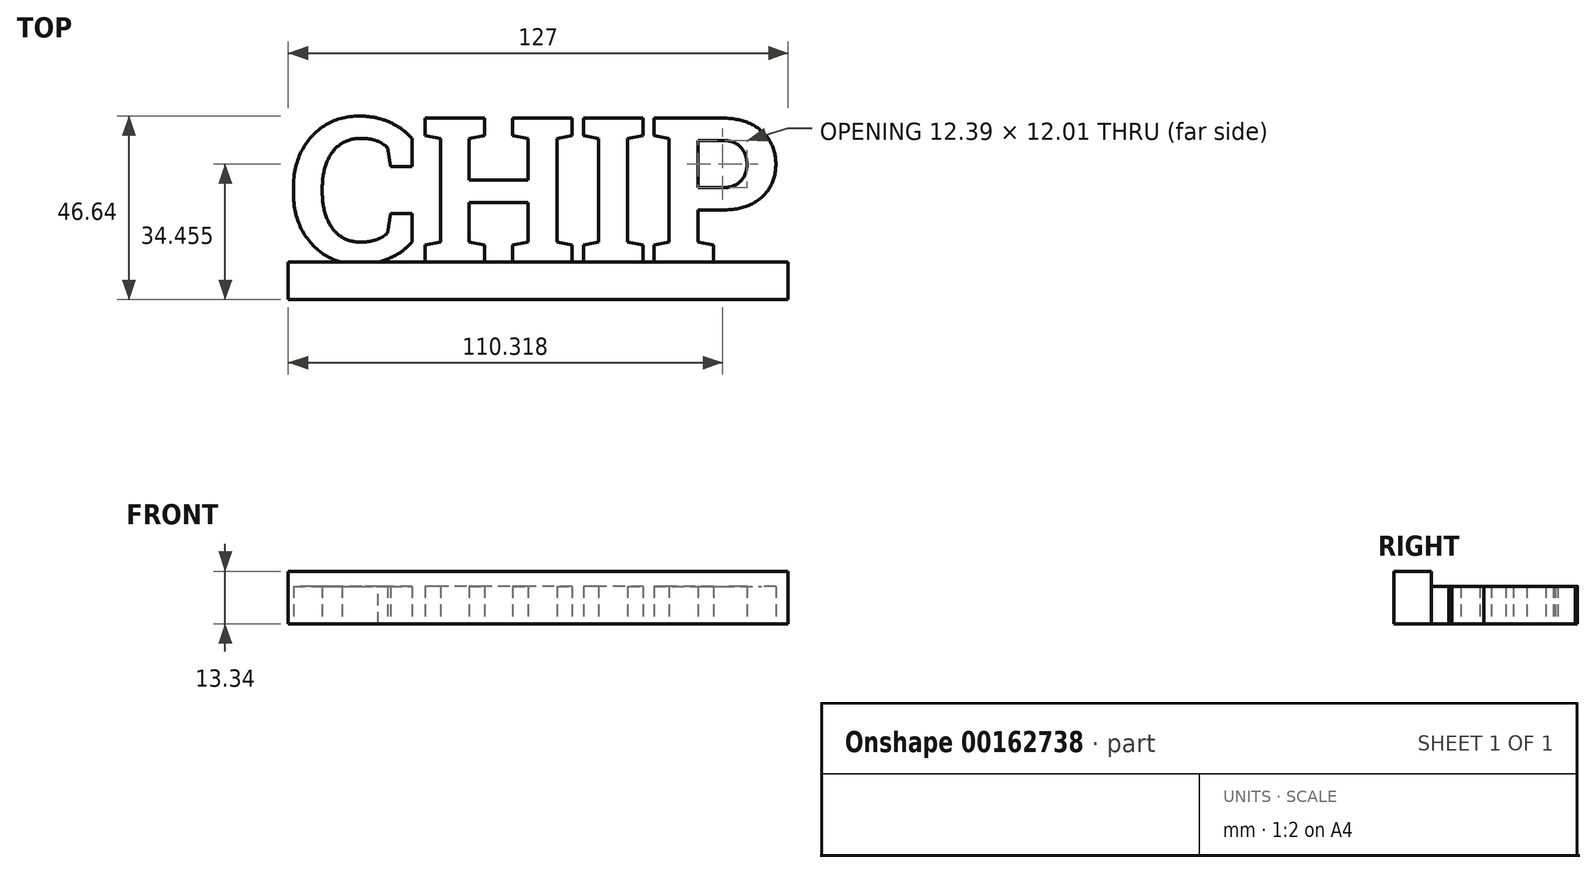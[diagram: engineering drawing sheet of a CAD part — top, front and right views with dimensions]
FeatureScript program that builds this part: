
annotation { "Feature Type Name" : "Feature", "Feature Type Description" : "" }
export const myFeature = defineFeature(function(context is Context, id is Id, definition is map)
    precondition{}
    {
        {
            var Q0;
            Q0=qCreatedBy(makeId("Top.planeOp"),FACE);
            var sketch = newSketch(context, id + "F0", { "sketchPlane" : qUnion([Q0])});
            skLineSegment(sketch, "E0.bottom", {"start": v(0, 0) * mm, "end": v(127, 0) * mm});
            skLineSegment(sketch, "E0.top", {"start": v(0, 9.53) * mm, "end": v(127, 9.53) * mm});
            skLineSegment(sketch, "E0.left", {"start": v(0, 0) * mm, "end": v(0, 9.53) * mm});
            skLineSegment(sketch, "E0.right", {"start": v(127, 0) * mm, "end": v(127, 9.53) * mm});
            skText(sketch, "E1", { "text": "CHIP", "fontName": "RobotoSlab-Bold.ttf"});
            const initialGuessF0  = {"E1": [0, 0.00953, 1, 0, 0.03705]};
            skSetInitialGuess(sketch, initialGuessF0);
            skSolve(sketch);
        }
        {
            var Q0;
            Q0 = qSketchRegion(id + "F0", true);
            extrude(context, id + "F1", {"entities" : qUnion([Q0]), "depth" : 9.52 * mm});
        }
        {
            var Q0;
            Q0=makeQuery(id+"F1.opExtrude","CAP_FACE",FACE,{"disambiguationData":[OSD([sQuery(id+"F0.wireOp",EDGE,"E0.bottom"),sQuery(id+"F0.wireOp",EDGE,"E0.top"),sQuery(id+"F0.wireOp",EDGE,"E0.left"),sQuery(id+"F0.wireOp",EDGE,"E0.right"),sQuery(id+"F0.wireOp",EDGE,"E1.sketch_text.stroke-0"),sQuery(id+"F0.wireOp",EDGE,"E1.sketch_text.stroke-1"),sQuery(id+"F0.wireOp",EDGE,"E1.sketch_text.stroke-2"),sQuery(id+"F0.wireOp",EDGE,"E1.sketch_text.stroke-3"),sQuery(id+"F0.wireOp",EDGE,"E1.sketch_text.stroke-4"),sQuery(id+"F0.wireOp",EDGE,"E1.sketch_text.stroke-5"),sQuery(id+"F0.wireOp",EDGE,"E1.sketch_text.stroke-6"),sQuery(id+"F0.wireOp",EDGE,"E1.sketch_text.stroke-7"),sQuery(id+"F0.wireOp",EDGE,"E1.sketch_text.stroke-8"),sQuery(id+"F0.wireOp",EDGE,"E1.sketch_text.stroke-9"),sQuery(id+"F0.wireOp",EDGE,"E1.sketch_text.stroke-10"),sQuery(id+"F0.wireOp",EDGE,"E1.sketch_text.stroke-11"),sQuery(id+"F0.wireOp",EDGE,"E1.sketch_text.stroke-12"),sQuery(id+"F0.wireOp",EDGE,"E1.sketch_text.stroke-13"),sQuery(id+"F0.wireOp",EDGE,"E1.sketch_text.stroke-14"),sQuery(id+"F0.wireOp",EDGE,"E1.sketch_text.stroke-15"),sQuery(id+"F0.wireOp",EDGE,"E1.sketch_text.stroke-16"),sQuery(id+"F0.wireOp",EDGE,"E1.sketch_text.stroke-17"),sQuery(id+"F0.wireOp",EDGE,"E1.sketch_text.stroke-18"),sQuery(id+"F0.wireOp",EDGE,"E1.sketch_text.stroke-19"),sQuery(id+"F0.wireOp",EDGE,"E1.sketch_text.stroke-20"),sQuery(id+"F0.wireOp",EDGE,"E1.sketch_text.stroke-21"),sQuery(id+"F0.wireOp",EDGE,"E1.sketch_text.stroke-22"),sQuery(id+"F0.wireOp",EDGE,"E1.sketch_text.stroke-23"),sQuery(id+"F0.wireOp",EDGE,"E1.sketch_text.stroke-24"),sQuery(id+"F0.wireOp",EDGE,"E1.sketch_text.stroke-25"),sQuery(id+"F0.wireOp",EDGE,"E1.sketch_text.stroke-26"),sQuery(id+"F0.wireOp",EDGE,"E1.sketch_text.stroke-27"),sQuery(id+"F0.wireOp",EDGE,"E1.sketch_text.stroke-28"),sQuery(id+"F0.wireOp",EDGE,"E1.sketch_text.stroke-29"),sQuery(id+"F0.wireOp",EDGE,"E1.sketch_text.stroke-30"),sQuery(id+"F0.wireOp",EDGE,"E1.sketch_text.stroke-31"),sQuery(id+"F0.wireOp",EDGE,"E1.sketch_text.stroke-32"),sQuery(id+"F0.wireOp",EDGE,"E1.sketch_text.stroke-33"),sQuery(id+"F0.wireOp",EDGE,"E1.sketch_text.stroke-34"),sQuery(id+"F0.wireOp",EDGE,"E1.sketch_text.stroke-35"),sQuery(id+"F0.wireOp",EDGE,"E1.sketch_text.stroke-36"),sQuery(id+"F0.wireOp",EDGE,"E1.sketch_text.stroke-37"),sQuery(id+"F0.wireOp",EDGE,"E1.sketch_text.stroke-38"),sQuery(id+"F0.wireOp",EDGE,"E1.sketch_text.stroke-39"),sQuery(id+"F0.wireOp",EDGE,"E1.sketch_text.stroke-40"),sQuery(id+"F0.wireOp",EDGE,"E1.sketch_text.stroke-42"),sQuery(id+"F0.wireOp",EDGE,"E1.sketch_text.stroke-43"),sQuery(id+"F0.wireOp",EDGE,"E1.sketch_text.stroke-44"),sQuery(id+"F0.wireOp",EDGE,"E1.sketch_text.stroke-45"),sQuery(id+"F0.wireOp",EDGE,"E1.sketch_text.stroke-46"),sQuery(id+"F0.wireOp",EDGE,"E1.sketch_text.stroke-47"),sQuery(id+"F0.wireOp",EDGE,"E1.sketch_text.stroke-48"),sQuery(id+"F0.wireOp",EDGE,"E1.sketch_text.stroke-50"),sQuery(id+"F0.wireOp",EDGE,"E1.sketch_text.stroke-51"),sQuery(id+"F0.wireOp",EDGE,"E1.sketch_text.stroke-52"),sQuery(id+"F0.wireOp",EDGE,"E1.sketch_text.stroke-53"),sQuery(id+"F0.wireOp",EDGE,"E1.sketch_text.stroke-54"),sQuery(id+"F0.wireOp",EDGE,"E1.sketch_text.stroke-55"),sQuery(id+"F0.wireOp",EDGE,"E1.sketch_text.stroke-56"),sQuery(id+"F0.wireOp",EDGE,"E1.sketch_text.stroke-57"),sQuery(id+"F0.wireOp",EDGE,"E1.sketch_text.stroke-58"),sQuery(id+"F0.wireOp",EDGE,"E1.sketch_text.stroke-59"),sQuery(id+"F0.wireOp",EDGE,"E1.sketch_text.stroke-60"),sQuery(id+"F0.wireOp",EDGE,"E1.sketch_text.stroke-62"),sQuery(id+"F0.wireOp",EDGE,"E1.sketch_text.stroke-63"),sQuery(id+"F0.wireOp",EDGE,"E1.sketch_text.stroke-64"),sQuery(id+"F0.wireOp",EDGE,"E1.sketch_text.stroke-65"),sQuery(id+"F0.wireOp",EDGE,"E1.sketch_text.stroke-66"),sQuery(id+"F0.wireOp",EDGE,"E1.sketch_text.stroke-67"),sQuery(id+"F0.wireOp",EDGE,"E1.sketch_text.stroke-68"),sQuery(id+"F0.wireOp",EDGE,"E1.sketch_text.stroke-69"),sQuery(id+"F0.wireOp",EDGE,"E1.sketch_text.stroke-70"),sQuery(id+"F0.wireOp",EDGE,"E1.sketch_text.stroke-71"),sQuery(id+"F0.wireOp",EDGE,"E1.sketch_text.stroke-72"),sQuery(id+"F0.wireOp",EDGE,"E1.sketch_text.stroke-73"),sQuery(id+"F0.wireOp",EDGE,"E1.sketch_text.stroke-75"),sQuery(id+"F0.wireOp",EDGE,"E1.sketch_text.stroke-76"),sQuery(id+"F0.wireOp",EDGE,"E1.sketch_text.stroke-77"),sQuery(id+"F0.wireOp",EDGE,"E1.sketch_text.stroke-78"),sQuery(id+"F0.wireOp",EDGE,"E1.sketch_text.stroke-79"),sQuery(id+"F0.wireOp",EDGE,"E1.sketch_text.stroke-80"),sQuery(id+"F0.wireOp",EDGE,"E1.sketch_text.stroke-81"),sQuery(id+"F0.wireOp",EDGE,"E1.sketch_text.stroke-82"),sQuery(id+"F0.wireOp",EDGE,"E1.sketch_text.stroke-83"),sQuery(id+"F0.wireOp",EDGE,"E1.sketch_text.stroke-84"),sQuery(id+"F0.wireOp",EDGE,"E1.sketch_text.stroke-85"),sQuery(id+"F0.wireOp",EDGE,"E1.sketch_text.stroke-86"),sQuery(id+"F0.wireOp",EDGE,"E1.sketch_text.stroke-87"),sQuery(id+"F0.wireOp",EDGE,"E1.sketch_text.stroke-88")])],"isStart":false});
            var sketch = newSketch(context, id + "F2", { "sketchPlane" : qUnion([Q0])});
            skLineSegment(sketch, "E2.bottom", {"start": v(0, 0) * mm, "end": v(127, 0) * mm});
            skLineSegment(sketch, "E2.top", {"start": v(0, 9.53) * mm, "end": v(127, 9.53) * mm});
            skLineSegment(sketch, "E2.left", {"start": v(0, 0) * mm, "end": v(0, 9.53) * mm});
            skLineSegment(sketch, "E2.right", {"start": v(127, 0) * mm, "end": v(127, 9.53) * mm});
            skSolve(sketch);
        }
        {
            var Q0;
            Q0 = qSketchRegion(id + "F2", true);
            extrude(context, id + "F3", {"entities" : qUnion([Q0]), "operationType" : NewBodyOperationType.ADD, "depth" : 3.8 * mm});
        }
    });
